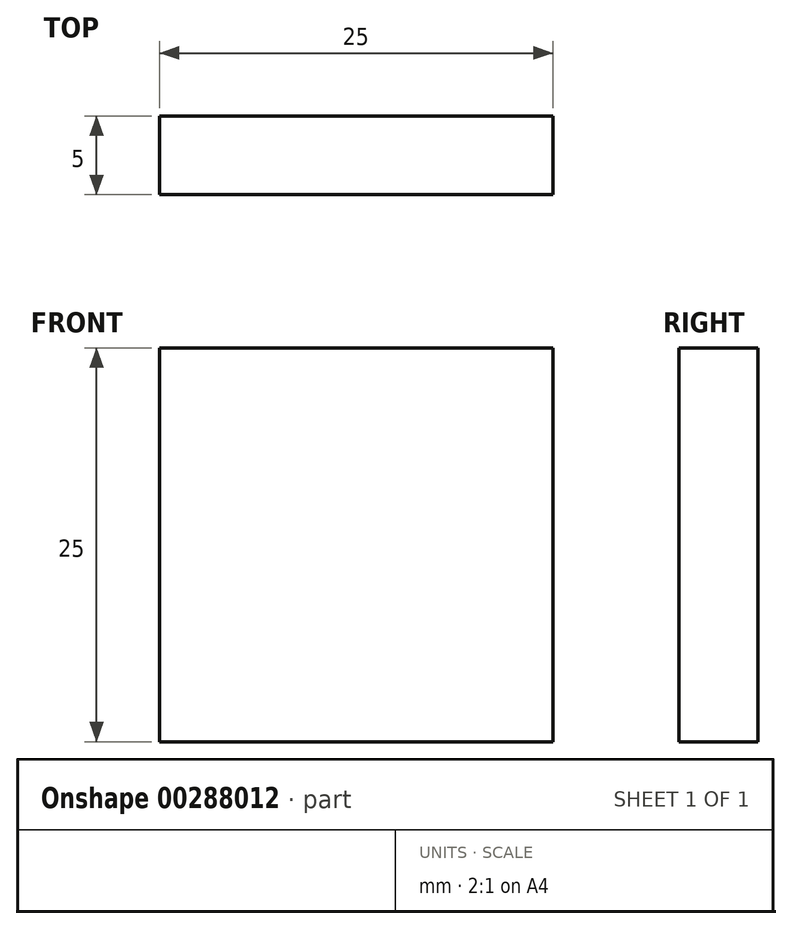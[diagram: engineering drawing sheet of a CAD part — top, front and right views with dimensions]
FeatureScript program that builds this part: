
annotation { "Feature Type Name" : "Feature", "Feature Type Description" : "" }
export const myFeature = defineFeature(function(context is Context, id is Id, definition is map)
    precondition{}
    {
        {
            var Q0;
            Q0=qCreatedBy(makeId("Front.planeOp"),FACE);
            var sketch = newSketch(context, id + "F0", { "sketchPlane" : qUnion([Q0])});
            skLineSegment(sketch, "E0.bottom", {"start": v(12.5, 12.5) * mm, "end": v(-12.5, 12.5) * mm});
            skLineSegment(sketch, "E0.top", {"start": v(12.5, -12.5) * mm, "end": v(-12.5, -12.5) * mm});
            skLineSegment(sketch, "E0.left", {"start": v(12.5, 12.5) * mm, "end": v(12.5, -12.5) * mm});
            skLineSegment(sketch, "E0.right", {"start": v(-12.5, 12.5) * mm, "end": v(-12.5, -12.5) * mm});
            skPoint(sketch, "E0.middle", {"position": v(0, 0) * mm});
            skSolve(sketch);
        }
        {
            var Q0;
            Q0=makeQuery(id+"F0.imprint","IMPRINT",FACE,{"disambiguationData":[TD([[makeQuery(id+"F0.imprint","IMPRINT",EDGE,{"derivedFrom":sQuery(id+"F0.wireOp",EDGE,"E0.bottom")}),1.0]])]});
            extrude(context, id + "F1", {"entities" : qUnion([Q0]), "endBound" : BoundingType.SYMMETRIC, "depth" : 5 * mm});
        }
    });
